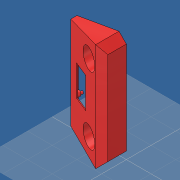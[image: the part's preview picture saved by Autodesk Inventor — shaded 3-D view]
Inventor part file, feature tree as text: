
AUTODESK INVENTOR PART (.ipt)
format: ipt  version: 2019 (Build 230136000, 136)  size: 259,584 bytes
history: native  units: mm
features: extrude x10, sketch x4, shell x1, hole x1, fillet x1, projected_geometry x1
ambient origin geometry x8: Origin, YZ Plane, XZ Plane, XY Plane, X Axis, Y Axis, Z Axis, Center Point
bodies: Volumenkörper1 (feature_tree)
feature tree (18):
  sketch  "Skizze2"  dims[d0=40.0mm d2=75.0mm d3=0.0mm d4=1.2mm]
  extrude  "Extrusion1"  Depth=1.2mm TaperAngle=0.0deg
  shell  "Wandung1"  Thickness=1.2mm
  sketch  "Skizze3"  dims[d12=27.75mm d13=2.0mm d16=75.0mm d17=0.0mm d20=2.0mm d21=0.0mm]
  extrude  "Extrusion2"  Depth=2.0mm TaperAngle=0.0deg
  extrude  "Extrusion4"  Depth=2.0mm TaperAngle=0.0deg
  extrude  "Extrusion11"  Depth=1.0mm
  extrude  "Extrusion15"  Depth=5.0mm
  sketch  "Skizze5"  dims[d30=16.0mm d34=2.0mm d35=0.0mm]
  extrude  "Extrusion7"  Depth=15.0mm
  extrude  "Extrusion8"  Depth=6.0mm
  extrude  "Extrusion10"  Depth=5.0mm
  hole  "Bohrung1"  [1 undecoded]
  sketch  "Skizze6"  dims[d36=2.0mm d37=0.0mm d38=1.0mm d40=5.0mm d43=15.0mm d45=6.0mm d46=21.816616mm d47=7.0mm d48=5.0mm d49=2.2mm d50=6.0mm d51=4.0mm d52=2.0mm d53=90.0deg d54=6.0mm d55=0.0mm d56=5.0mm d59=2.0mm d60=0.0mm d63=2.5mm d66=28.0mm d67=19.3mm d68=26.75mm d69=23.5mm d70=23.5mm d71=2.25mm d72=2.25mm d73=4.5mm d74=4.0mm d75=4.0mm d76=0.0mm d77=14.0mm d80=6.0mm d81=21.816616mm d82=0.0mm d83=1.0mm d84=0.0mm d87=1.0mm d88=0.0mm d90=0.5mm d91=0.5mm d92=0.0mm d93=5.0mm d94=1.0mm d95=1.0mm d96=5.0mm]
  extrude  "Extrusion12"  Depth=5.0mm
  extrude  "Extrusion14"  Depth=5.0mm
  fillet  "Rundung1"  Radius=2.0mm
  projected_geometry  "Projizierte Kontur1"
note: 1 required parameter value undecoded (feature->parameter linkage not recoverable at this tier; creation-order binding heuristic only, values carry confidence <= 0.55)
